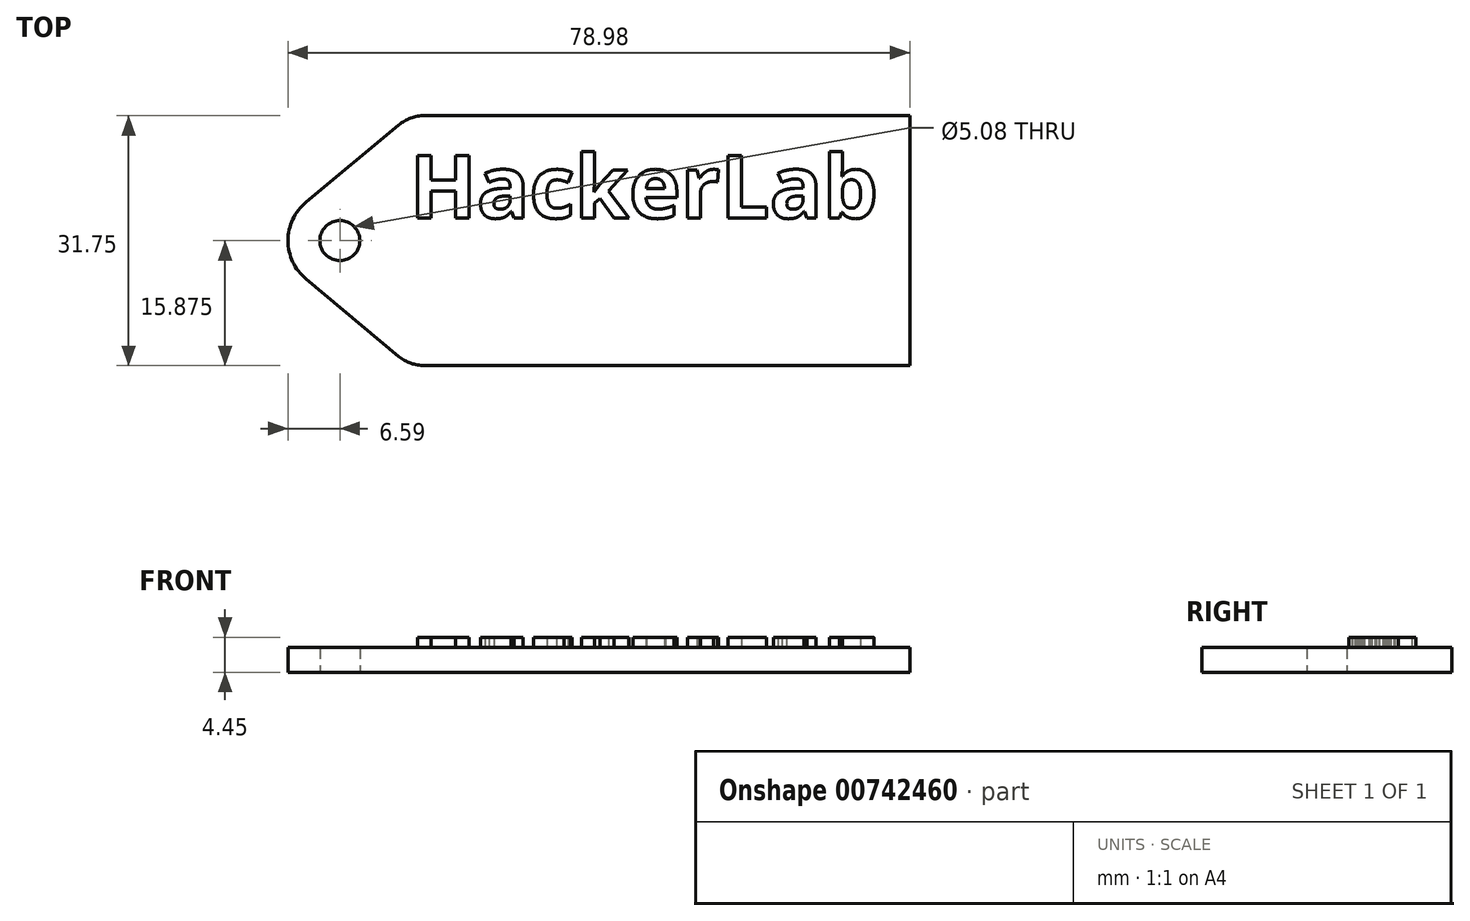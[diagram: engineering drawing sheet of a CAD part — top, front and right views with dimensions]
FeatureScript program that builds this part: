
annotation { "Feature Type Name" : "Feature", "Feature Type Description" : "" }
export const myFeature = defineFeature(function(context is Context, id is Id, definition is map)
    precondition{}
    {
        {
            var Q0;
            Q0=qCreatedBy(makeId("Top.planeOp"),FACE);
            var sketch = newSketch(context, id + "F0", { "sketchPlane" : qUnion([Q0])});
            skLineSegment(sketch, "E0.bottom", {"start": v(0, 0) * mm, "end": v(63.5, 0) * mm});
            skLineSegment(sketch, "E0.top", {"start": v(0, 31.75) * mm, "end": v(63.5, 31.75) * mm});
            skLineSegment(sketch, "E0.left", {"start": v(0, 0) * mm, "end": v(0, 31.75) * mm});
            skLineSegment(sketch, "E0.right", {"start": v(63.5, 0) * mm, "end": v(63.5, 31.75) * mm});
            skLineSegment(sketch, "E1", {"start": v(0, 0) * mm, "end": v(-13.2, 11) * mm});
            skPoint(sketch, "E1.endSnap0", {"position": v(0, 15.88) * mm});
            skLineSegment(sketch, "E2", {"start": v(-13.2, 20.75) * mm, "end": v(0, 31.75) * mm});
            skCircle(sketch, "E3", {"center": v(-8.9, 15.88) * mm, "radius": 2.54 * mm});
            skPoint(sketch, "E4.visualSharp", {"position": v(-19.05, 15.88) * mm});
            skArc(sketch, "E4.filletArc", {"start": v(-13.2, 20.75) * mm, "mid": v(-15.48, 15.88) * mm, "end": v(-13.2, 11) * mm});
            skSolve(sketch);
        }
        {
            var Q0;
            Q0 = qSketchRegion(id + "F0", true);
            extrude(context, id + "F1", {"entities" : qUnion([Q0]), "depth" : 3.17 * mm, "offsetDistance" : 25.4 * mm});
        }
        {
            var Q0;
            Q0=makeQuery(id+"F1.opExtrude","SWEPT_EDGE",EDGE,{"disambiguationData":[OSD([sQuery(id+"F0.wireOp",EDGE,"E0.top"),sQuery(id+"F0.wireOp",EDGE,"E0.left"),sQuery(id+"F0.wireOp",EDGE,"E2")])]});
            var Q1;
            Q1=makeQuery(id+"F1.opExtrude","SWEPT_EDGE",EDGE,{"disambiguationData":[OSD([sQuery(id+"F0.wireOp",EDGE,"E0.bottom"),sQuery(id+"F0.wireOp",EDGE,"E0.left"),sQuery(id+"F0.wireOp",EDGE,"E1")])]});
            fillet(context, id + "F2", {"entities" : qUnion([Q0, Q1]), "radius" : 5.08 * mm, "tangentPropagation" : true, "allowEdgeOverflow" : false});
        }
        {
            var Q0;
            Q0=makeQuery(id+"F1.opExtrude","CAP_FACE",FACE,{"disambiguationData":[OSD([sQuery(id+"F0.wireOp",EDGE,"E0.bottom"),sQuery(id+"F0.wireOp",EDGE,"E0.top"),sQuery(id+"F0.wireOp",EDGE,"E0.right"),sQuery(id+"F0.wireOp",EDGE,"E1"),sQuery(id+"F0.wireOp",EDGE,"E2"),sQuery(id+"F0.wireOp",EDGE,"E3"),sQuery(id+"F0.wireOp",EDGE,"E4.filletArc")])],"isStart":false});
            var sketch = newSketch(context, id + "F3", { "sketchPlane" : qUnion([Q0])});
            skText(sketch, "E5", { "text": "HackerLab", "fontName": "OpenSans-Bold.ttf"});
            const initialGuessF3  = {"E5": [0, 0.01876, 1, 0, 0.008]};
            skSetInitialGuess(sketch, initialGuessF3);
            skSolve(sketch);
        }
        {
            var Q0;
            Q0 = qSketchRegion(id + "F3", true);
            extrude(context, id + "F4", {"entities" : qUnion([Q0]), "operationType" : NewBodyOperationType.ADD, "depth" : 1.27 * mm, "offsetDistance" : 25.4 * mm});
        }
    });
